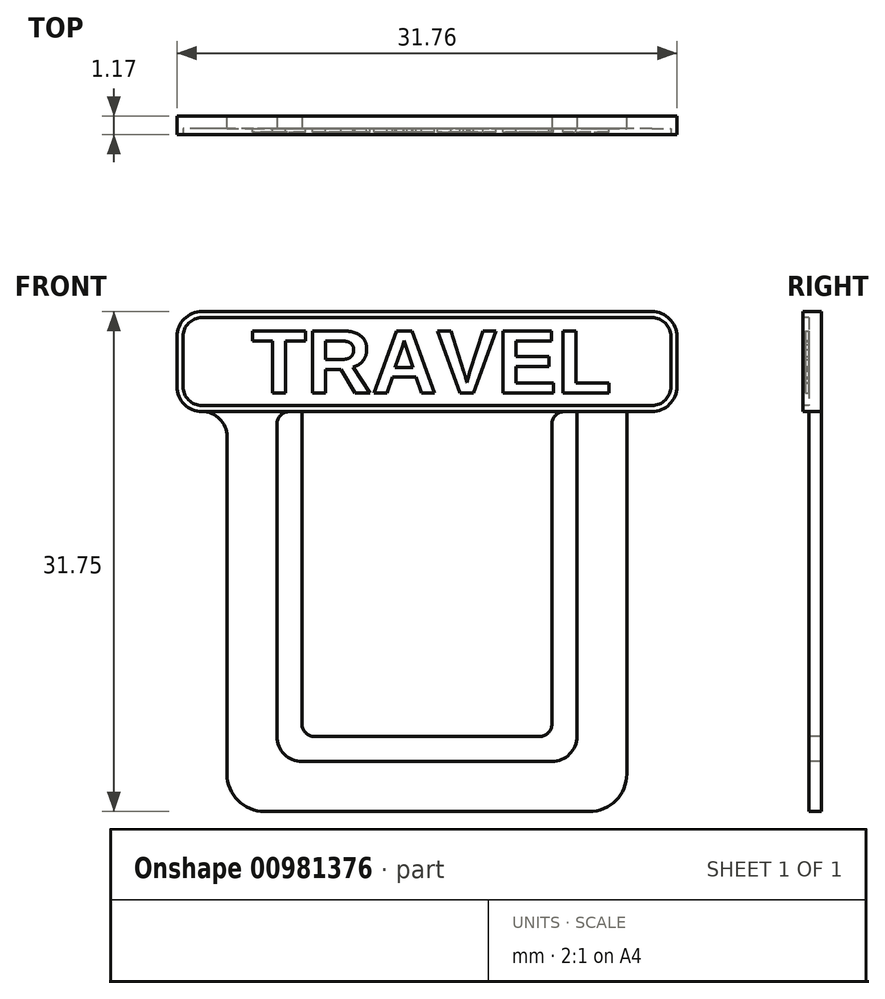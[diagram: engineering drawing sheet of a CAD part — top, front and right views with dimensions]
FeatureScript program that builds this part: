
annotation { "Feature Type Name" : "Feature", "Feature Type Description" : "" }
export const myFeature = defineFeature(function(context is Context, id is Id, definition is map)
    precondition{}
    {
        {
            var Q0;
            Q0=qCreatedBy(makeId("Front.planeOp"),FACE);
            var sketch = newSketch(context, id + "F0", { "sketchPlane" : qUnion([Q0])});
            skLineSegment(sketch, "E0.bottom", {"start": v(12.7, 12.7) * mm, "end": v(-12.7, 12.7) * mm});
            skLineSegment(sketch, "E0.top", {"start": v(12.7, -12.7) * mm, "end": v(-12.7, -12.7) * mm});
            skLineSegment(sketch, "E0.left", {"start": v(12.7, 12.7) * mm, "end": v(12.7, -12.7) * mm});
            skLineSegment(sketch, "E0.right", {"start": v(-12.7, 12.7) * mm, "end": v(-12.7, -12.7) * mm});
            skPoint(sketch, "E0.middle", {"position": v(0, 0) * mm});
            skSolve(sketch);
        }
        {
            var Q0;
            Q0=makeQuery(id+"F0.imprint","IMPRINT",FACE,{"disambiguationData":[TD([[makeQuery(id+"F0.imprint","IMPRINT",EDGE,{"derivedFrom":sQuery(id+"F0.wireOp",EDGE,"E0.bottom")}),1.0]])]});
            extrude(context, id + "F1", {"entities" : qUnion([Q0]), "depth" : 0.8 * mm, "offsetDistance" : 25.4 * mm});
        }
        {
            var Q0;
            Q0=makeQuery(id+"F1.opExtrude","SWEPT_EDGE",EDGE,{"disambiguationData":[OSD([sQuery(id+"F0.wireOp",EDGE,"E0.top"),sQuery(id+"F0.wireOp",EDGE,"E0.left")])]});
            var Q1;
            Q1=makeQuery(id+"F1.opExtrude","SWEPT_EDGE",EDGE,{"disambiguationData":[OSD([sQuery(id+"F0.wireOp",EDGE,"E0.top"),sQuery(id+"F0.wireOp",EDGE,"E0.right")])]});
            fillet(context, id + "F2", {"entities" : qUnion([Q0, Q1]), "radius" : 2.38 * mm, "tangentPropagation" : true, "allowEdgeOverflow" : false});
        }
        {
            var Q0;
            Q0=makeQuery(id+"F1.opExtrude","CAP_FACE",FACE,{"disambiguationData":[OSD([sQuery(id+"F0.wireOp",EDGE,"E0.bottom"),sQuery(id+"F0.wireOp",EDGE,"E0.top"),sQuery(id+"F0.wireOp",EDGE,"E0.left"),sQuery(id+"F0.wireOp",EDGE,"E0.right")])],"isStart":false});
            var sketch = newSketch(context, id + "F3", { "sketchPlane" : qUnion([Q0])});
            skLineSegment(sketch, "E1.bottom", {"start": v(9.52, 12.7) * mm, "end": v(-9.53, 12.7) * mm});
            skLineSegment(sketch, "E1.top", {"start": v(9.53, -9.53) * mm, "end": v(-9.52, -9.53) * mm});
            skLineSegment(sketch, "E1.left", {"start": v(9.52, 12.7) * mm, "end": v(9.53, -9.53) * mm});
            skLineSegment(sketch, "E1.right", {"start": v(-9.53, 12.7) * mm, "end": v(-9.52, -9.53) * mm});
            skPoint(sketch, "E1.middle", {"position": v(0, 0) * mm});
            skSolve(sketch);
        }
        {
            var Q0;
            Q0=makeQuery(id+"F3.imprint","IMPRINT",FACE,{"disambiguationData":[TD([[makeQuery(id+"F3.imprint","IMPRINT",EDGE,{"derivedFrom":sQuery(id+"F3.wireOp",EDGE,"E1.bottom")}),1.0]])]});
            extrude(context, id + "F4", {"entities" : qUnion([Q0]), "operationType" : NewBodyOperationType.REMOVE, "oppositeDirection" : true, "depth" : 4.93 * mm, "offsetDistance" : 25.4 * mm});
        }
        {
            var Q0;
            Q0=makeQuery(id+"F1.opExtrude","CAP_FACE",FACE,{"disambiguationData":[OSD([sQuery(id+"F0.wireOp",EDGE,"E0.bottom"),sQuery(id+"F0.wireOp",EDGE,"E0.top"),sQuery(id+"F0.wireOp",EDGE,"E0.left"),sQuery(id+"F0.wireOp",EDGE,"E0.right")])],"isStart":false});
            var sketch = newSketch(context, id + "F5", { "sketchPlane" : qUnion([Q0])});
            skLineSegment(sketch, "E2.bottom", {"start": v(-15.88, 12.7) * mm, "end": v(15.88, 12.7) * mm});
            skLineSegment(sketch, "E2.top", {"start": v(-15.88, 19.05) * mm, "end": v(15.88, 19.05) * mm});
            skLineSegment(sketch, "E2.left", {"start": v(-15.88, 12.7) * mm, "end": v(-15.88, 19.05) * mm});
            skLineSegment(sketch, "E2.right", {"start": v(15.87, 12.7) * mm, "end": v(15.87, 19.05) * mm});
            skSolve(sketch);
        }
        {
            var Q0;
            Q0=makeQuery(id+"F5.imprint","IMPRINT",FACE,{"disambiguationData":[TD([[makeQuery(id+"F5.imprint","IMPRINT",EDGE,{"derivedFrom":sQuery(id+"F5.wireOp",EDGE,"E2.top")}),-1.0]])]});
            extrude(context, id + "F6", {"entities" : qUnion([Q0]), "operationType" : NewBodyOperationType.ADD, "oppositeDirection" : true, "depth" : 0.8 * mm, "offsetDistance" : 25.4 * mm});
        }
        {
            var Q0;
            Q0=makeQuery(id+"F6.opExtrude","SWEPT_EDGE",EDGE,{"disambiguationData":[OSD([sQuery(id+"F5.wireOp",EDGE,"E2.top"),sQuery(id+"F5.wireOp",EDGE,"E2.left")])]});
            var Q1;
            Q1=makeQuery(id+"F6.opExtrude","SWEPT_EDGE",EDGE,{"disambiguationData":[OSD([sQuery(id+"F5.wireOp",EDGE,"E2.top"),sQuery(id+"F5.wireOp",EDGE,"E2.right")])]});
            var Q2;
            Q2=makeQuery(id+"F6.opExtrude","SWEPT_EDGE",EDGE,{"disambiguationData":[OSD([sQuery(id+"F5.wireOp",EDGE,"E2.bottom"),sQuery(id+"F5.wireOp",EDGE,"E2.right")])]});
            var Q3;
            Q3=makeQuery(id+"F1.opExtrude","SWEPT_EDGE",EDGE,{"disambiguationData":[OSD([sQuery(id+"F0.wireOp",EDGE,"E0.bottom"),sQuery(id+"F0.wireOp",EDGE,"E0.left")])]});
            var Q4;
            Q4=makeQuery(id+"F6.opExtrude","SWEPT_EDGE",EDGE,{"disambiguationData":[OSD([sQuery(id+"F5.wireOp",EDGE,"E2.bottom"),sQuery(id+"F5.wireOp",EDGE,"E2.left")])]});
            var Q5;
            Q5=makeQuery(id+"F1.opExtrude","SWEPT_EDGE",EDGE,{"disambiguationData":[OSD([sQuery(id+"F0.wireOp",EDGE,"E0.bottom"),sQuery(id+"F0.wireOp",EDGE,"E0.right")])]});
            fillet(context, id + "F7", {"entities" : qUnion([Q0, Q1, Q2, Q3, Q4, Q5]), "radius" : 1.59 * mm, "tangentPropagation" : true, "allowEdgeOverflow" : false});
        }
        {
            var Q0;
            Q0=makeQuery(id+"F4.boolean.opBoolean","COPY",EDGE,{"derivedFrom":makeQuery(id+"F4.opExtrude","SWEPT_EDGE",EDGE,{"disambiguationData":[OSD([sQuery(id+"F3.wireOp",EDGE,"E1.top"),sQuery(id+"F3.wireOp",EDGE,"E1.right")])]})});
            var Q1;
            Q1=makeQuery(id+"F4.boolean.opBoolean","COPY",EDGE,{"derivedFrom":makeQuery(id+"F4.opExtrude","SWEPT_EDGE",EDGE,{"disambiguationData":[OSD([sQuery(id+"F3.wireOp",EDGE,"E1.top"),sQuery(id+"F3.wireOp",EDGE,"E1.left")])]})});
            fillet(context, id + "F8", {"entities" : qUnion([Q0, Q1]), "radius" : 1.59 * mm, "tangentPropagation" : true, "allowEdgeOverflow" : false});
        }
        {
            var Q0;
            Q0=makeQuery(id+"F6.boolean.opBoolean","MERGE",FACE,{"derivedFrom":[makeQuery(id+"F1.opExtrude","CAP_FACE",FACE,{"disambiguationData":[OSD([sQuery(id+"F0.wireOp",EDGE,"E0.bottom"),sQuery(id+"F0.wireOp",EDGE,"E0.top"),sQuery(id+"F0.wireOp",EDGE,"E0.left"),sQuery(id+"F0.wireOp",EDGE,"E0.right")])],"isStart":false}),makeQuery(id+"F6.opExtrude","CAP_FACE",FACE,{"disambiguationData":[OSD([sQuery(id+"F5.wireOp",EDGE,"E2.bottom"),sQuery(id+"F5.wireOp",EDGE,"E2.top"),sQuery(id+"F5.wireOp",EDGE,"E2.left"),sQuery(id+"F5.wireOp",EDGE,"E2.right")])],"isStart":true})]});
            var sketch = newSketch(context, id + "F9", { "sketchPlane" : qUnion([Q0])});
            skLineSegment(sketch, "E3.bottom", {"start": v(-7.94, 12.7) * mm, "end": v(7.94, 12.7) * mm});
            skLineSegment(sketch, "E3.top", {"start": v(-7.94, -7.94) * mm, "end": v(7.94, -7.94) * mm});
            skLineSegment(sketch, "E3.left", {"start": v(-7.94, 12.7) * mm, "end": v(-7.94, -7.94) * mm});
            skLineSegment(sketch, "E3.right", {"start": v(7.94, 12.7) * mm, "end": v(7.94, -7.94) * mm});
            skSolve(sketch);
        }
        {
            var Q0;
            Q0=makeQuery(id+"F9.imprint","IMPRINT",FACE,{"disambiguationData":[TD([[makeQuery(id+"F9.imprint","IMPRINT",EDGE,{"derivedFrom":sQuery(id+"F9.wireOp",EDGE,"E3.bottom")}),1.0]])]});
            extrude(context, id + "F10", {"entities" : qUnion([Q0]), "operationType" : NewBodyOperationType.ADD, "oppositeDirection" : true, "depth" : 0.8 * mm, "offsetDistance" : 25.4 * mm});
        }
        {
            var Q0;
            Q0=makeQuery(id+"F10.opExtrude","SWEPT_EDGE",EDGE,{"disambiguationData":[OSD([sQuery(id+"F5.wireOp",EDGE,"E2.bottom"),sQuery(id+"F9.wireOp",EDGE,"E3.bottom"),sQuery(id+"F9.wireOp",EDGE,"E3.left")])]});
            var Q1;
            Q1=makeQuery(id+"F4.boolean.opBoolean","COPY",EDGE,{"derivedFrom":makeQuery(id+"F4.opExtrude","SWEPT_EDGE",EDGE,{"disambiguationData":[OSD([sQuery(id+"F0.wireOp",EDGE,"E0.bottom"),sQuery(id+"F3.wireOp",EDGE,"E1.bottom"),sQuery(id+"F3.wireOp",EDGE,"E1.right")])]})});
            var Q2;
            Q2=makeQuery(id+"F10.opExtrude","SWEPT_EDGE",EDGE,{"disambiguationData":[OSD([sQuery(id+"F5.wireOp",EDGE,"E2.bottom"),sQuery(id+"F9.wireOp",EDGE,"E3.bottom"),sQuery(id+"F9.wireOp",EDGE,"E3.right")])]});
            var Q3;
            Q3=makeQuery(id+"F4.boolean.opBoolean","COPY",EDGE,{"derivedFrom":makeQuery(id+"F4.opExtrude","SWEPT_EDGE",EDGE,{"disambiguationData":[OSD([sQuery(id+"F0.wireOp",EDGE,"E0.bottom"),sQuery(id+"F3.wireOp",EDGE,"E1.bottom"),sQuery(id+"F3.wireOp",EDGE,"E1.left")])]})});
            fillet(context, id + "F11", {"entities" : qUnion([Q0, Q1, Q2, Q3]), "radius" : 0.8 * mm, "tangentPropagation" : true, "allowEdgeOverflow" : false});
        }
        {
            var Q0;
            Q0=makeQuery(id+"F10.opExtrude","SWEPT_EDGE",EDGE,{"disambiguationData":[OSD([sQuery(id+"F9.wireOp",EDGE,"E3.top"),sQuery(id+"F9.wireOp",EDGE,"E3.left")])]});
            var Q1;
            Q1=makeQuery(id+"F10.opExtrude","SWEPT_EDGE",EDGE,{"disambiguationData":[OSD([sQuery(id+"F9.wireOp",EDGE,"E3.top"),sQuery(id+"F9.wireOp",EDGE,"E3.right")])]});
            fillet(context, id + "F12", {"entities" : qUnion([Q0, Q1]), "radius" : 0.8 * mm, "tangentPropagation" : true, "allowEdgeOverflow" : false});
        }
        {
            var Q0;
            Q0=makeQuery(id+"F10.boolean.opBoolean","MERGE",FACE,{"derivedFrom":[makeQuery(id+"F6.boolean.opBoolean","MERGE",FACE,{"derivedFrom":[makeQuery(id+"F1.opExtrude","CAP_FACE",FACE,{"disambiguationData":[OSD([sQuery(id+"F0.wireOp",EDGE,"E0.bottom"),sQuery(id+"F0.wireOp",EDGE,"E0.top"),sQuery(id+"F0.wireOp",EDGE,"E0.left"),sQuery(id+"F0.wireOp",EDGE,"E0.right")])],"isStart":false}),makeQuery(id+"F6.opExtrude","CAP_FACE",FACE,{"disambiguationData":[OSD([sQuery(id+"F5.wireOp",EDGE,"E2.bottom"),sQuery(id+"F5.wireOp",EDGE,"E2.top"),sQuery(id+"F5.wireOp",EDGE,"E2.left"),sQuery(id+"F5.wireOp",EDGE,"E2.right")])],"isStart":true})]}),makeQuery(id+"F10.opExtrude","CAP_FACE",FACE,{"disambiguationData":[OSD([sQuery(id+"F9.wireOp",EDGE,"E3.bottom"),sQuery(id+"F9.wireOp",EDGE,"E3.top"),sQuery(id+"F9.wireOp",EDGE,"E3.left"),sQuery(id+"F9.wireOp",EDGE,"E3.right")])],"isStart":true})]});
            var sketch = newSketch(context, id + "F13", { "sketchPlane" : qUnion([Q0])});
            skArc(sketch, "E4.0", {"start": v(-14.29, 19.05) * mm, "mid": v(-15.41, 18.59) * mm, "end": v(-15.88, 17.46) * mm});
            skLineSegment(sketch, "E5.0", {"start": v(-15.88, 14.29) * mm, "end": v(-15.88, 17.46) * mm});
            skArc(sketch, "E6.0", {"start": v(-15.88, 14.29) * mm, "mid": v(-15.41, 13.16) * mm, "end": v(-14.29, 12.7) * mm});
            skLineSegment(sketch, "E7.0", {"start": v(-14.29, 19.05) * mm, "end": v(14.29, 19.05) * mm});
            skArc(sketch, "E8.0", {"start": v(15.87, 17.46) * mm, "mid": v(15.41, 18.59) * mm, "end": v(14.29, 19.05) * mm});
            skLineSegment(sketch, "E9.0", {"start": v(15.87, 14.29) * mm, "end": v(15.87, 17.46) * mm});
            skArc(sketch, "E10.0", {"start": v(14.29, 12.7) * mm, "mid": v(15.41, 13.16) * mm, "end": v(15.87, 14.29) * mm});
            skLineSegment(sketch, "E11", {"start": v(-14.29, 12.7) * mm, "end": v(14.29, 12.7) * mm});
            skSolve(sketch);
        }
        {
            var Q0;
            Q0=makeQuery(id+"F13.imprint","IMPRINT",FACE,{"disambiguationData":[TD([[makeQuery(id+"F13.imprint","IMPRINT",EDGE,{"derivedFrom":sQuery(id+"F13.wireOp",EDGE,"E4.0")}),1.0]])]});
            extrude(context, id + "F14", {"entities" : qUnion([Q0]), "operationType" : NewBodyOperationType.ADD, "depth" : 0.38 * mm, "offsetDistance" : 25.4 * mm});
        }
        {
            var Q0;
            Q0=makeQuery(id+"F14.opExtrude","CAP_FACE",FACE,{"disambiguationData":[OSD([sQuery(id+"F13.wireOp",EDGE,"E4.0"),sQuery(id+"F13.wireOp",EDGE,"E5.0"),sQuery(id+"F13.wireOp",EDGE,"E6.0"),sQuery(id+"F13.wireOp",EDGE,"E7.0"),sQuery(id+"F13.wireOp",EDGE,"E8.0"),sQuery(id+"F13.wireOp",EDGE,"E9.0"),sQuery(id+"F13.wireOp",EDGE,"E10.0"),sQuery(id+"F13.wireOp",EDGE,"E11")])],"isStart":false});
            var sketch = newSketch(context, id + "F15", { "sketchPlane" : qUnion([Q0])});
            skArc(sketch, "E12.0", {"start": v(-14.29, 19.05) * mm, "mid": v(-15.41, 18.59) * mm, "end": v(-15.88, 17.46) * mm});
            skLineSegment(sketch, "E13.0", {"start": v(-14.29, 19.05) * mm, "end": v(14.29, 19.05) * mm});
            skLineSegment(sketch, "E14.0", {"start": v(-15.88, 14.29) * mm, "end": v(-15.88, 17.46) * mm});
            skArc(sketch, "E15.0", {"start": v(-15.88, 14.29) * mm, "mid": v(-15.41, 13.16) * mm, "end": v(-14.29, 12.7) * mm});
            skLineSegment(sketch, "E16.0", {"start": v(-14.29, 12.7) * mm, "end": v(14.29, 12.7) * mm});
            skArc(sketch, "E17.0", {"start": v(14.29, 12.7) * mm, "mid": v(15.41, 13.16) * mm, "end": v(15.87, 14.29) * mm});
            skArc(sketch, "E18.0", {"start": v(15.87, 17.46) * mm, "mid": v(15.41, 18.59) * mm, "end": v(14.29, 19.05) * mm});
            skArc(sketch, "E19", {"start": v(-14.29, 18.67) * mm, "mid": v(-15.14, 18.32) * mm, "end": v(-15.5, 17.46) * mm});
            skArc(sketch, "E20", {"start": v(-15.5, 14.29) * mm, "mid": v(-15.14, 13.43) * mm, "end": v(-14.29, 13.08) * mm});
            skArc(sketch, "E21", {"start": v(15.5, 17.46) * mm, "mid": v(15.14, 18.32) * mm, "end": v(14.29, 18.67) * mm});
            skArc(sketch, "E22", {"start": v(14.29, 13.08) * mm, "mid": v(15.14, 13.43) * mm, "end": v(15.5, 14.29) * mm});
            skLineSegment(sketch, "E23", {"start": v(-14.29, 19.05) * mm, "end": v(-14.29, 12.7) * mm, "construction": true});
            skLineSegment(sketch, "E24", {"start": v(-15.88, 17.46) * mm, "end": v(15.87, 17.46) * mm, "construction": true});
            skLineSegment(sketch, "E25", {"start": v(14.29, 19.05) * mm, "end": v(14.29, 12.7) * mm, "construction": true});
            skLineSegment(sketch, "E26", {"start": v(15.87, 14.29) * mm, "end": v(-15.88, 14.29) * mm, "construction": true});
            skLineSegment(sketch, "E27", {"start": v(14.29, 18.67) * mm, "end": v(-14.29, 18.67) * mm});
            skLineSegment(sketch, "E28", {"start": v(-15.5, 17.46) * mm, "end": v(-15.5, 14.29) * mm});
            skLineSegment(sketch, "E29", {"start": v(-14.29, 13.08) * mm, "end": v(14.29, 13.08) * mm});
            skLineSegment(sketch, "E30", {"start": v(15.5, 17.46) * mm, "end": v(15.5, 14.29) * mm});
            skSolve(sketch);
        }
        {
            var Q0;
            Q0=makeQuery(id+"F15.imprint","IMPRINT",FACE,{"disambiguationData":[TD([[makeQuery(id+"F15.imprint","IMPRINT",EDGE,{"derivedFrom":sQuery(id+"F15.wireOp",EDGE,"E19")}),1.0]])]});
            var Q1;
            {var subQ0=sQuery(id+"F9.wireOp",EDGE,"E3.right");var subQ1=sQuery(id+"F9.wireOp",EDGE,"E3.top");var subQ3=sQuery(id+"F0.wireOp",EDGE,"E0.bottom");var subQ4=sQuery(id+"F9.wireOp",EDGE,"E3.left");var subQ5=makeQuery(id+"F6.opExtrude","CAP_FACE",FACE,{"disambiguationData":[OSD([sQuery(id+"F5.wireOp",EDGE,"E2.bottom"),sQuery(id+"F5.wireOp",EDGE,"E2.top"),sQuery(id+"F5.wireOp",EDGE,"E2.left"),sQuery(id+"F5.wireOp",EDGE,"E2.right")])],"isStart":true});var subQ6=makeQuery(id+"F1.opExtrude","CAP_FACE",FACE,{"disambiguationData":[OSD([subQ3,sQuery(id+"F0.wireOp",EDGE,"E0.top"),sQuery(id+"F0.wireOp",EDGE,"E0.left"),sQuery(id+"F0.wireOp",EDGE,"E0.right")])],"isStart":false});var subQ7=makeQuery(id+"F10.opExtrude","CAP_FACE",FACE,{"disambiguationData":[OSD([sQuery(id+"F9.wireOp",EDGE,"E3.bottom"),subQ1,subQ4,subQ0])],"isStart":true});Q1=makeQuery(id+"F14.boolean.opBoolean","SPLIT",FACE,{"disambiguationData":[TD([makeQuery(id+"F10.opExtrude","SWEPT_FACE",FACE,{"disambiguationData":[OSD([subQ1])]})])],"derivedFrom":makeQuery(id+"F10.boolean.opBoolean","MERGE",FACE,{"derivedFrom":[makeQuery(id+"F6.boolean.opBoolean","MERGE",FACE,{"derivedFrom":[subQ6,subQ5]}),subQ7]})});}
            extrude(context, id + "F16", {"entities" : qUnion([Q0]), "operationType" : NewBodyOperationType.REMOVE, "endBound" : BoundingType.UP_TO_SURFACE, "oppositeDirection" : true, "depth" : 25.4 * mm, "endBoundEntityFace" : qUnion([Q1]), "offsetDistance" : 25.4 * mm});
        }
        {
            var Q0;
            Q0=qCreatedBy(makeId("Front.planeOp"),FACE);
            var sketch = newSketch(context, id + "F17", { "sketchPlane" : qUnion([Q0])});
            skText(sketch, "E31", { "text": "TRAVEL", "fontName": "Arimo-Bold.ttf"});
            const initialGuessF17  = {"E31": [-0.01114, 0.01388, 1, 0, 0.00412]};
            skSetInitialGuess(sketch, initialGuessF17);
            skSolve(sketch);
        }
        {
            var Q0;
            Q0=qSketchRegion(id+"F17",true);
            extrude(context, id + "F18", {"entities" : qUnion([Q0]), "operationType" : NewBodyOperationType.ADD, "depth" : 1.02 * mm, "offsetDistance" : 25.4 * mm});
        }
    });
